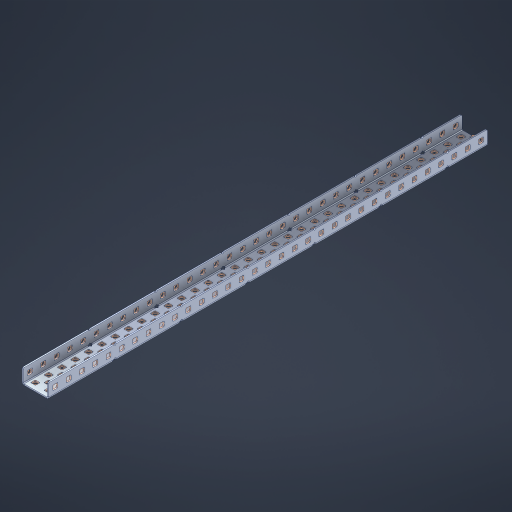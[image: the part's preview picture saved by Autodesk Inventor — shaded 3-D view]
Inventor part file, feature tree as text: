
AUTODESK INVENTOR PART (.ipt)
format: ipt  version: 2023 (Build 270158000, 158)  size: 2,011,648 bytes
history: native  units: in
note: dims shown in document units (in); Inventor stores cm internally (conversion verified against a paired STEP export)
features: other x172, extrude x163, sheet_metal_op x11, sketch x10, pattern_linear x2, mirror x1, chamfer x1
ambient origin geometry x8: Origin, YZ Plane, XZ Plane, XY Plane, X Axis, Y Axis, Z Axis, Center Point
bodies: Solid1 (feature_tree), Body (feature_tree)
feature tree (360):
  sheet_metal_op  "Flanges"
  other  "Flange Pattern Plane"
  other  "Flange Pattern Sketch"
  sheet_metal_op  "Flange Pattern"
  sheet_metal_op  "Body Pattern"
  pattern_linear  "Center Pattern"  Spacing1=0.0469in  [1 undecoded]
  other  "Arc Length"
  mirror  "Notch Mirror"
  pattern_linear  "Notch Pattern"  Spacing1=0.182in  [1 undecoded]
  chamfer  "End Chamfer"
  extrude  "Half Cut"  Depth=0.02in
  sketch  "Sketch1"  dims[d0=1.0in]
  other  "Plate1"
  sketch  "Sketch2"  dims[d1=16.5in]
  other  "Plate2"
  sheet_metal_op  "Bend1"
  sheet_metal_op  "Corner1"
  sketch  "Sketch3"  dims[d2=0.0469in]
  sketch  "Sketch7"  dims[d3=0.0469in]
  other  "Srf1"
  other  "Srf2"
  sketch  "Sketch8"  dims[d4=0.0234in]
  sketch  "Sketch9"  dims[d5=0.0938in]
  other  "Srf91"
  sheet_metal_op  "Body Pattern Sketch"
  other  "Srf92"
  sketch  "Sketch13"  dims[d6=0.0469in]
  sketch  "Sketch14"  dims[d7=0.5in d8=90.0deg d9=0.0312in]
  sketch  "Sketch15"  dims[d10=0.1875in]
  sketch  "Sketch16"  dims[d11=0.0469in d12=0.0469in d16=0.182in d17=0.02in d18=0.0469in d19=0.0in d20=0.25in d21=0.25in d38=12.9921in d40=0.5in d41=0.7874in d43=1.0in d46=0.172in d47=1.0in d48=0.0in d49=0.182in d50=0.02in d51=0.25in d52=0.25in d53=0.0469in d54=0.0in d55=0.172in d56=1.0in d57=0.0in d58=0.25in d60=12.9921in d62=0.5in d63=0.7874in d65=0.5in d85=0.1227in d86=0.1659in d88=0.04in d89=0.0469in d90=0.0in d91=0.04in d92=0.0491in d95=2.5in d96=0.04in d97=0.25in d98=45.0deg d99=0.25in d100=0.5in d101=0.0in d102=2.497in d106=0.182in d107=0.02in d108=0.5in d109=0.5in d110=0.0469in d111=0.0in d112=0.172in d113=0.5in d114=0.0in d117=0.5in d118=0.5in d119=0.5in]
  other  "Srf786"
  other  "Srf823"
  other  "Srf824"
  other  "Srf825"
  other  "Srf826"
  other  "Srf827"
  other  "Srf828"
  other  "Srf829"
  other  "Srf856"
  other  "Srf857"
  other  "Srf858"
  other  "Srf859"
  other  "Srf860"
  other  "Srf861"
  other  "Srf862"
  other  "Srf889"
  other  "Srf890"
  other  "Srf891"
  other  "Srf892"
  other  "Srf893"
  other  "Srf894"
  other  "Srf895"
  other  "Srf896"
  other  "Srf922"
  other  "Srf923"
  other  "Srf924"
  other  "Srf925"
  other  "Srf926"
  other  "Srf959"
  other  "Srf960"
  other  "Srf961"
  other  "Srf962"
  other  "Srf963"
  other  "Srf996"
  other  "Srf997"
  other  "Srf998"
  other  "Srf999"
  other  "Srf1000"
  other  "Srf1143"
  other  "Srf1144"
  other  "Srf1145"
  other  "Srf1146"
  other  "Srf1147"
  other  "Srf1148"
  other  "Srf1149"
  other  "Srf1150"
  other  "Srf1151"
  other  "Srf1152"
  other  "Srf1153"
  other  "Srf1154"
  other  "Srf1155"
  other  "Srf1156"
  other  "Srf1157"
  other  "Srf1158"
  other  "Srf1159"
  other  "Srf1160"
  other  "Srf1161"
  other  "Srf1162"
  other  "Srf1163"
  other  "Srf1164"
  other  "Srf1165"
  other  "Srf1166"
  other  "Srf1167"
  other  "Srf1168"
  other  "Srf1169"
  other  "Srf1170"
  other  "Srf1171"
  other  "Srf1172"
  other  "Srf1173"
  other  "Srf1174"
  other  "Srf1175"
  other  "Srf1176"
  other  "Srf1177"
  other  "Srf1178"
  other  "Srf1179"
  other  "Srf1180"
  other  "Srf1181"
  other  "Srf1182"
  other  "Srf1183"
  other  "Srf1184"
  other  "Srf1185"
  other  "Srf1186"
  other  "Srf1187"
  other  "Srf1188"
  other  "Srf1189"
  other  "Srf1190"
  other  "Srf1191"
  other  "Srf1192"
  other  "Srf1193"
  other  "Srf1194"
  other  "Srf1199"
  other  "Srf1200"
  other  "Srf1201"
  other  "Srf1202"
  other  "Srf1203"
  other  "Srf1204"
  other  "Srf1205"
  other  "Srf1206"
  other  "Srf1207"
  other  "Srf1208"
  other  "Srf1209"
  other  "Srf1210"
  other  "Srf1211"
  other  "Srf1212"
  other  "Srf1213"
  other  "Srf1214"
  other  "Srf1215"
  other  "Srf1216"
  other  "Srf1217"
  other  "Srf1218"
  other  "Srf1219"
  other  "Srf1220"
  other  "Srf1221"
  other  "Srf1222"
  other  "Srf1223"
  other  "Srf1224"
  other  "Srf1225"
  other  "Srf1226"
  other  "Srf1227"
  other  "Srf1228"
  other  "Srf1229"
  other  "Srf1230"
  other  "Srf1231"
  other  "Srf1232"
  other  "Srf1233"
  other  "Srf1234"
  other  "Srf1235"
  other  "Srf1236"
  other  "Srf1237"
  other  "Srf1238"
  other  "Srf1239"
  other  "Srf1240"
  other  "Srf1241"
  other  "Srf1242"
  other  "Srf1243"
  other  "Srf1244"
  other  "Srf1245"
  other  "Srf1246"
  other  "Srf1247"
  other  "Srf1248"
  other  "Srf1249"
  other  "Srf1250"
  other  "Srf1255"
  other  "Srf1256"
  other  "Srf1257"
  other  "Srf1258"
  other  "Srf1259"
  other  "Srf1260"
  other  "Srf1261"
  other  "Srf1262"
  other  "Srf1263"
  other  "Srf1264"
  other  "Srf1265"
  other  "Srf1266"
  other  "Srf1267"
  other  "Srf1268"
  other  "Srf1269"
  other  "Srf1270"
  other  "Srf1271"
  other  "Srf1272"
  other  "Srf1273"
  sheet_metal_op  "Flange Stamp"
  sheet_metal_op  "Flange Circle"
  sheet_metal_op  "Body Stamp"
  sheet_metal_op  "Body Circle"
  other  "Center Stamp"
  other  "Center Circle"
  sheet_metal_op  "Notch"
  extrude  "ExtrusionSrf2"  Depth=0.0469in
  extrude  "ExtrusionSrf92"  TaperAngle=0.0deg  [1 undecoded]
  extrude  "ExtrusionSrf823"  Depth=0.5in
  extrude  "ExtrusionSrf824"  Depth=0.5in
  extrude  "ExtrusionSrf825"  Depth=0.5in
  extrude  "ExtrusionSrf826"  Depth=0.5in
  extrude  "ExtrusionSrf827"  Depth=1.0in TaperAngle=0.0deg
  extrude  "ExtrusionSrf828"  Depth=0.5in
  extrude  "ExtrusionSrf829"  Depth=0.02in
  extrude  "ExtrusionSrf856"  Depth=0.5in
  extrude  "ExtrusionSrf857"  Depth=0.5in
  extrude  "ExtrusionSrf858"  Depth=0.0469in
  extrude  "ExtrusionSrf859"  TaperAngle=0.0deg  [1 undecoded]
  extrude  "ExtrusionSrf860"  Depth=0.5in
  extrude  "ExtrusionSrf861"  Depth=1.0in TaperAngle=0.0deg
  extrude  "ExtrusionSrf862"  Depth=0.5in
  extrude  "ExtrusionSrf889"  Depth=0.5in
  extrude  "ExtrusionSrf890"  Depth=0.5in
  extrude  "ExtrusionSrf891"  Depth=0.5in
  extrude  "ExtrusionSrf892"  Depth=0.5in
  extrude  "ExtrusionSrf893"  Depth=0.5in
  extrude  "ExtrusionSrf894"  Depth=0.0469in
  extrude  "ExtrusionSrf895"  TaperAngle=0.0deg  [1 undecoded]
  extrude  "ExtrusionSrf896"  Depth=0.5in
  extrude  "ExtrusionSrf922"  Depth=0.5in
  extrude  "ExtrusionSrf923"  Depth=2.5in
  extrude  "ExtrusionSrf924"  Depth=0.5in TaperAngle=45.0deg
  extrude  "ExtrusionSrf925"  Depth=0.5in
  extrude  "ExtrusionSrf926"  Depth=0.5in TaperAngle=0.0deg
  extrude  "ExtrusionSrf959"  Depth=0.5in
  extrude  "ExtrusionSrf960"  Depth=0.5in
  extrude  "ExtrusionSrf961"  Depth=0.02in
  extrude  "ExtrusionSrf962"  Depth=0.5in
  extrude  "ExtrusionSrf963"  Depth=0.5in
  extrude  "ExtrusionSrf996"  Depth=0.0469in
  extrude  "ExtrusionSrf997"  TaperAngle=0.0deg  [1 undecoded]
  extrude  "ExtrusionSrf998"  Depth=0.5in
  extrude  "ExtrusionSrf999"  Depth=0.5in TaperAngle=0.0deg
  extrude  "ExtrusionSrf1000"  Depth=0.5in
  extrude  "ExtrusionSrf1143"  Depth=0.5in
  extrude  "ExtrusionSrf1144"  Depth=0.5in
  extrude  "ExtrusionSrf1145"  [1 undecoded]
  extrude  "ExtrusionSrf1146"  [1 undecoded]
  extrude  "ExtrusionSrf1147"  [1 undecoded]
  extrude  "ExtrusionSrf1148"  [1 undecoded]
  extrude  "ExtrusionSrf1149"  [1 undecoded]
  extrude  "ExtrusionSrf1150"  [1 undecoded]
  extrude  "ExtrusionSrf1151"  [1 undecoded]
  extrude  "ExtrusionSrf1152"  [1 undecoded]
  extrude  "ExtrusionSrf1153"  [1 undecoded]
  extrude  "ExtrusionSrf1154"  [1 undecoded]
  extrude  "ExtrusionSrf1155"  [1 undecoded]
  extrude  "ExtrusionSrf1156"  [1 undecoded]
  extrude  "ExtrusionSrf1157"  [1 undecoded]
  extrude  "ExtrusionSrf1158"  [1 undecoded]
  extrude  "ExtrusionSrf1159"  [1 undecoded]
  extrude  "ExtrusionSrf1160"  [1 undecoded]
  extrude  "ExtrusionSrf1161"  [1 undecoded]
  extrude  "ExtrusionSrf1162"  [1 undecoded]
  extrude  "ExtrusionSrf1163"  [1 undecoded]
  extrude  "ExtrusionSrf1164"  [1 undecoded]
  extrude  "ExtrusionSrf1165"  [1 undecoded]
  extrude  "ExtrusionSrf1166"  [1 undecoded]
  extrude  "ExtrusionSrf1167"  [1 undecoded]
  extrude  "ExtrusionSrf1168"  [1 undecoded]
  extrude  "ExtrusionSrf1169"  [1 undecoded]
  extrude  "ExtrusionSrf1170"  [1 undecoded]
  extrude  "ExtrusionSrf1171"  [1 undecoded]
  extrude  "ExtrusionSrf1172"  [1 undecoded]
  extrude  "ExtrusionSrf1173"  [1 undecoded]
  extrude  "ExtrusionSrf1174"  [1 undecoded]
  extrude  "ExtrusionSrf1175"  [1 undecoded]
  extrude  "ExtrusionSrf1176"  [1 undecoded]
  extrude  "ExtrusionSrf1177"  [1 undecoded]
  extrude  "ExtrusionSrf1178"  [1 undecoded]
  extrude  "ExtrusionSrf1179"  [1 undecoded]
  extrude  "ExtrusionSrf1180"  [1 undecoded]
  extrude  "ExtrusionSrf1181"  [1 undecoded]
  extrude  "ExtrusionSrf1182"  [1 undecoded]
  extrude  "ExtrusionSrf1183"  [1 undecoded]
  extrude  "ExtrusionSrf1184"  [1 undecoded]
  extrude  "ExtrusionSrf1185"  [1 undecoded]
  extrude  "ExtrusionSrf1186"  [1 undecoded]
  extrude  "ExtrusionSrf1187"  [1 undecoded]
  extrude  "ExtrusionSrf1188"  [1 undecoded]
  extrude  "ExtrusionSrf1189"  [1 undecoded]
  extrude  "ExtrusionSrf1190"  [1 undecoded]
  extrude  "ExtrusionSrf1191"  [1 undecoded]
  extrude  "ExtrusionSrf1192"  [1 undecoded]
  extrude  "ExtrusionSrf1193"  [1 undecoded]
  extrude  "ExtrusionSrf1194"  [1 undecoded]
  extrude  "ExtrusionSrf1199"  [1 undecoded]
  extrude  "ExtrusionSrf1200"  [1 undecoded]
  extrude  "ExtrusionSrf1201"  [1 undecoded]
  extrude  "ExtrusionSrf1202"  [1 undecoded]
  extrude  "ExtrusionSrf1203"  [1 undecoded]
  extrude  "ExtrusionSrf1204"  [1 undecoded]
  extrude  "ExtrusionSrf1205"  [1 undecoded]
  extrude  "ExtrusionSrf1206"  [1 undecoded]
  extrude  "ExtrusionSrf1207"  [1 undecoded]
  extrude  "ExtrusionSrf1208"  [1 undecoded]
  extrude  "ExtrusionSrf1209"  [1 undecoded]
  extrude  "ExtrusionSrf1210"  [1 undecoded]
  extrude  "ExtrusionSrf1211"  [1 undecoded]
  extrude  "ExtrusionSrf1212"  [1 undecoded]
  extrude  "ExtrusionSrf1213"  [1 undecoded]
  extrude  "ExtrusionSrf1214"  [1 undecoded]
  extrude  "ExtrusionSrf1215"  [1 undecoded]
  extrude  "ExtrusionSrf1216"  [1 undecoded]
  extrude  "ExtrusionSrf1217"  [1 undecoded]
  extrude  "ExtrusionSrf1218"  [1 undecoded]
  extrude  "ExtrusionSrf1219"  [1 undecoded]
  extrude  "ExtrusionSrf1220"  [1 undecoded]
  extrude  "ExtrusionSrf1221"  [1 undecoded]
  extrude  "ExtrusionSrf1222"  [1 undecoded]
  extrude  "ExtrusionSrf1223"  [1 undecoded]
  extrude  "ExtrusionSrf1224"  [1 undecoded]
  extrude  "ExtrusionSrf1225"  [1 undecoded]
  extrude  "ExtrusionSrf1226"  [1 undecoded]
  extrude  "ExtrusionSrf1227"  [1 undecoded]
  extrude  "ExtrusionSrf1228"  [1 undecoded]
  extrude  "ExtrusionSrf1229"  [1 undecoded]
  extrude  "ExtrusionSrf1230"  [1 undecoded]
  extrude  "ExtrusionSrf1231"  [1 undecoded]
  extrude  "ExtrusionSrf1232"  [1 undecoded]
  extrude  "ExtrusionSrf1233"  [1 undecoded]
  extrude  "ExtrusionSrf1234"  [1 undecoded]
  extrude  "ExtrusionSrf1235"  [1 undecoded]
  extrude  "ExtrusionSrf1236"  [1 undecoded]
  extrude  "ExtrusionSrf1237"  [1 undecoded]
  extrude  "ExtrusionSrf1238"  [1 undecoded]
  extrude  "ExtrusionSrf1239"  [1 undecoded]
  extrude  "ExtrusionSrf1240"  [1 undecoded]
  extrude  "ExtrusionSrf1241"  [1 undecoded]
  extrude  "ExtrusionSrf1242"  [1 undecoded]
  extrude  "ExtrusionSrf1243"  [1 undecoded]
  extrude  "ExtrusionSrf1244"  [1 undecoded]
  extrude  "ExtrusionSrf1245"  [1 undecoded]
  extrude  "ExtrusionSrf1246"  [1 undecoded]
  extrude  "ExtrusionSrf1247"  [1 undecoded]
  extrude  "ExtrusionSrf1248"  [1 undecoded]
  extrude  "ExtrusionSrf1249"  [1 undecoded]
  extrude  "ExtrusionSrf1250"  [1 undecoded]
  extrude  "ExtrusionSrf1255"  [1 undecoded]
  extrude  "ExtrusionSrf1256"  [1 undecoded]
  extrude  "ExtrusionSrf1257"  [1 undecoded]
  extrude  "ExtrusionSrf1258"  [1 undecoded]
  extrude  "ExtrusionSrf1259"  [1 undecoded]
  extrude  "ExtrusionSrf1260"  [1 undecoded]
  extrude  "ExtrusionSrf1261"  [1 undecoded]
  extrude  "ExtrusionSrf1262"  [1 undecoded]
  extrude  "ExtrusionSrf1263"  [1 undecoded]
  extrude  "ExtrusionSrf1264"  [1 undecoded]
  extrude  "ExtrusionSrf1265"  [1 undecoded]
  extrude  "ExtrusionSrf1266"  [1 undecoded]
  extrude  "ExtrusionSrf1267"  [1 undecoded]
  extrude  "ExtrusionSrf1268"  [1 undecoded]
  extrude  "ExtrusionSrf1269"  [1 undecoded]
  extrude  "ExtrusionSrf1270"  [1 undecoded]
  extrude  "ExtrusionSrf1271"  [1 undecoded]
  extrude  "ExtrusionSrf1272"  [1 undecoded]
  extrude  "ExtrusionSrf1273"  [1 undecoded]
note: 127 required parameter values undecoded (feature->parameter linkage not recoverable at this tier; creation-order binding heuristic only, values carry confidence <= 0.55)
